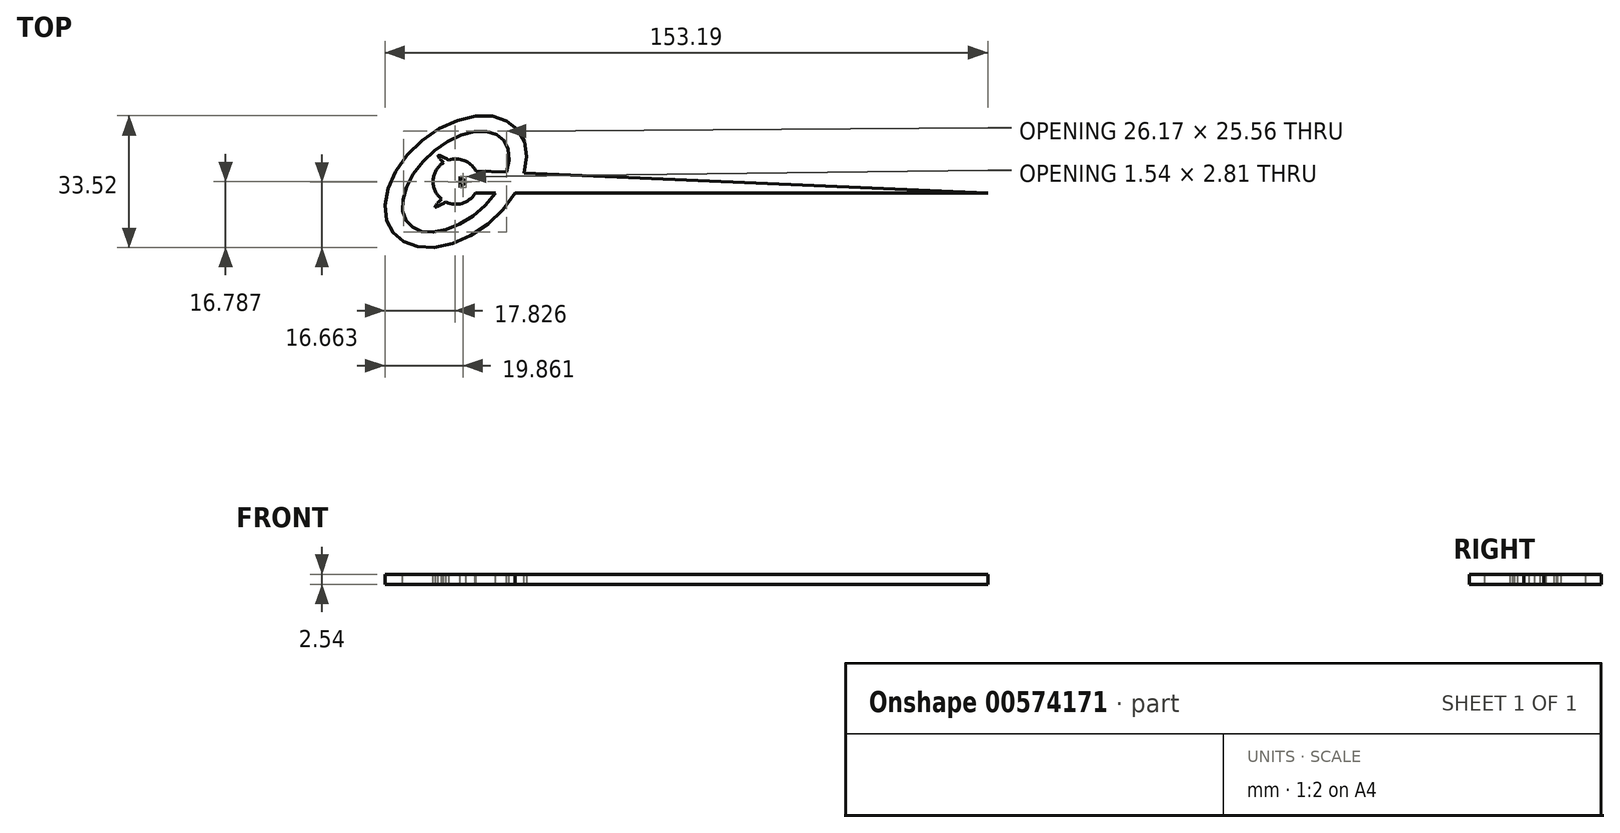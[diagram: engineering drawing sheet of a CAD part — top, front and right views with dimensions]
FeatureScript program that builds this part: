
annotation { "Feature Type Name" : "Feature", "Feature Type Description" : "" }
export const myFeature = defineFeature(function(context is Context, id is Id, definition is map)
    precondition{}
    {
        {
            var Q0;
            Q0=qCreatedBy(makeId("Top.planeOp"),FACE);
            var sketch = newSketch(context, id + "F0", { "sketchPlane" : qUnion([Q0])});
            skLineSegment(sketch, "E0", {"start": v(62.44, 29.81) * mm, "end": v(-67.53, 35.5) * mm});
            skPoint(sketch, "E1.first.point", {"position": v(-72.74, 32.77) * mm});
            skEllipse(sketch, "E2", {"center": v(-72.74, 32.77) * mm, "majorRadius": 20.56 * mm, "minorRadius": 13.51 * mm, "majorAxis": v(-0.77, -0.64)});
            skPoint(sketch, "E3.second.point.positionSnap0", {"position": v(-81.38, 43.15) * mm});
            skEllipse(sketch, "E4", {"center": v(-72.74, 32.77) * mm, "majorRadius": 16.1 * mm, "minorRadius": 9.5 * mm, "majorAxis": v(0.75, 0.67)});
            skFitSpline(sketch, "E5", {"points": [v(-75.87, 37.59) * mm, v(-77.22, 39.4) * mm, v(-74.5, 38.24) * mm], "startDerivative": vector(-4.75, 5.3) * mm, "endDerivative": vector(7.24, -3.82) * mm});
            skFitSpline(sketch, "E6", {"points": [v(-76.39, 28.33) * mm, v(-77.94, 26.33) * mm, v(-75.23, 27.6) * mm], "startDerivative": vector(-5.27, -5.74) * mm, "endDerivative": vector(7.4, 4.13) * mm});
            skLineSegment(sketch, "E7", {"start": v(-71.66, 31.27) * mm, "end": v(-71.66, 34.08) * mm});
            skLineSegment(sketch, "E8", {"start": v(-71.66, 34.08) * mm, "end": v(-70.12, 32.63) * mm});
            skLineSegment(sketch, "E9", {"start": v(-70.12, 32.63) * mm, "end": v(-71.66, 31.27) * mm});
            skLineSegment(sketch, "E10", {"start": v(-67.87, 29.71) * mm, "end": v(-67.64, 29.81) * mm});
            skLineSegment(sketch, "E11.trimOffspring", {"start": v(-67.64, 29.81) * mm, "end": v(62.44, 29.81) * mm});
            skLineSegment(sketch, "E12", {"start": v(-67.75, 35.62) * mm, "end": v(-67.53, 35.5) * mm});
            skArc(sketch, "E13.trimOffspring", {"start": v(-67.75, 35.62) * mm, "mid": v(-78.48, 32.88) * mm, "end": v(-67.87, 29.71) * mm});
            skPoint(sketch, "E14.orphan", {"position": v(-72.66, 35.72) * mm});
            skPoint(sketch, "E15.end.orphan", {"position": v(-72.8, 29.81) * mm});
            skPoint(sketch, "E16.2.internal.orphan", {"position": v(-70.12, 34.46) * mm});
            skPoint(sketch, "E16.startDerivative.orphan", {"position": v(-69.67, 32.96) * mm});
            skPoint(sketch, "E17.2.internal.orphan", {"position": v(-70.12, 30.79) * mm});
            skPoint(sketch, "E18.0.internal.orphan", {"position": v(-69.67, 32.63) * mm});
            skFitSpline(sketch, "E19", {"points": [v(-70.12, 32.63) * mm, v(-69.16, 33.4) * mm, v(-70.33, 34.86) * mm], "startDerivative": vector(3.09, 1.53) * mm, "endDerivative": vector(-3.29, 2.88) * mm});
            skFitSpline(sketch, "E20", {"points": [v(-70.12, 32.63) * mm, v(-69.25, 31.9) * mm, v(-70.23, 30.4) * mm], "startDerivative": vector(2.78, -1.4) * mm, "endDerivative": vector(-2.79, -3.01) * mm});
            skFitSpline(sketch, "E21", {"points": [v(-69.67, 32.63) * mm, v(-68.77, 32.02) * mm, v(-69.92, 30.03) * mm], "startDerivative": vector(3.05, -1.1) * mm, "endDerivative": vector(-3.15, -3.91) * mm});
            skFitSpline(sketch, "E22", {"points": [v(-69.67, 32.63) * mm, v(-68.82, 33.38) * mm, v(-70.2, 35.18) * mm], "startDerivative": vector(2.97, 1.56) * mm, "endDerivative": vector(-3.65, 3.43) * mm});
            skSolve(sketch);
        }
        {
            var Q0;
            {var subQ0=sQuery(id+"F0.wireOp",EDGE,"E0");var subQ1=sQuery(id+"F0.wireOp",EDGE,"IcqNIeTD-ZECF-q0YG-0frz-Qsa368bnDGnI");var subQ2=makeQuery(id+"F0.imprint","INTERSECT",VERTEX,{"derivedFrom":[subQ1,subQ0]});Q0=makeQuery(id+"F0.imprint","IMPRINT",FACE,{"disambiguationData":[TD([[makeQuery(id+"F0.imprint","IMPRINT",EDGE,{"disambiguationData":[TD([[subQ2,1.0]])],"derivedFrom":subQ1}),1.0]])]});}
            var Q1;
            {var subQ0=sQuery(id+"F0.wireOp",EDGE,"E2");var subQ1=sQuery(id+"F0.wireOp",EDGE,"IcqNIeTD-ZECF-q0YG-0frz-Qsa368bnDGnI");var subQ2=makeQuery(id+"F0.imprint","INTERSECT",VERTEX,{"derivedFrom":[subQ1,subQ0]});Q1=makeQuery(id+"F0.imprint","IMPRINT",FACE,{"disambiguationData":[TD([[makeQuery(id+"F0.imprint","IMPRINT",EDGE,{"disambiguationData":[TD([[subQ2,1.0]])],"derivedFrom":subQ1}),-1.0]])]});}
            var Q2;
            {var subQ0=sQuery(id+"F0.wireOp",EDGE,"E2");var subQ1=sQuery(id+"F0.wireOp",EDGE,"IcqNIeTD-ZECF-q0YG-0frz-Qsa368bnDGnI");var subQ2=makeQuery(id+"F0.imprint","INTERSECT",VERTEX,{"derivedFrom":[subQ1,subQ0]});Q2=makeQuery(id+"F0.imprint","IMPRINT",FACE,{"disambiguationData":[TD([[makeQuery(id+"F0.imprint","IMPRINT",EDGE,{"disambiguationData":[TD([[subQ2,1.0]])],"derivedFrom":subQ1}),1.0]])]});}
            var Q3;
            {var subQ0=sQuery(id+"F0.wireOp",EDGE,"YC09zkpM-6MoU-lyNe-iY1n-6Od7lSqIglm4");var subQ1=sQuery(id+"F0.wireOp",EDGE,"IcqNIeTD-ZECF-q0YG-0frz-Qsa368bnDGnI");var subQ2=makeQuery(id+"F0.imprint","INTERSECT",VERTEX,{"derivedFrom":[subQ1,subQ0]});Q3=makeQuery(id+"F0.imprint","IMPRINT",FACE,{"disambiguationData":[TD([[makeQuery(id+"F0.imprint","IMPRINT",EDGE,{"disambiguationData":[TD([[subQ2,-1.0]])],"derivedFrom":subQ1}),1.0]])]});}
            var Q4;
            {var subQ5=sQuery(id+"F0.wireOp",EDGE,"E15");Q4=makeQuery(id+"F0.imprint","IMPRINT",FACE,{"disambiguationData":[TD([[makeQuery(id+"F0.imprint","IMPRINT",EDGE,{"derivedFrom":subQ5}),-1.0]])]});}
            var Q5;
            {var subQ0=sQuery(id+"F0.wireOp",EDGE,"E5");Q5=makeQuery(id+"F0.imprint","IMPRINT",FACE,{"disambiguationData":[TD([[makeQuery(id+"F0.imprint","IMPRINT",EDGE,{"derivedFrom":subQ0}),-1.0]])]});}
            var Q6;
            {var subQ0=sQuery(id+"F0.wireOp",EDGE,"E6");Q6=makeQuery(id+"F0.imprint","IMPRINT",FACE,{"disambiguationData":[TD([[makeQuery(id+"F0.imprint","IMPRINT",EDGE,{"derivedFrom":subQ0}),1.0]])]});}
            var Q7;
            {var subQ0=sQuery(id+"F0.wireOp",EDGE,"E15");Q7=makeQuery(id+"F0.imprint","IMPRINT",FACE,{"disambiguationData":[TD([[makeQuery(id+"F0.imprint","IMPRINT",EDGE,{"derivedFrom":subQ0}),1.0]])]});}
            var Q8;
            {var subQ0=sQuery(id+"F0.wireOp",EDGE,"E2");var subQ1=sQuery(id+"F0.wireOp",EDGE,"E0");var subQ2=makeQuery(id+"F0.imprint","INTERSECT",VERTEX,{"derivedFrom":[subQ1,subQ0]});Q8=makeQuery(id+"F0.imprint","IMPRINT",FACE,{"disambiguationData":[TD([[makeQuery(id+"F0.imprint","IMPRINT",EDGE,{"disambiguationData":[TD([[subQ2,-1.0]])],"derivedFrom":subQ1}),-1.0]])]});}
            var Q9;
            {var subQ0=sQuery(id+"F0.wireOp",EDGE,"E2");var subQ1=sQuery(id+"F0.wireOp",EDGE,"E0");var subQ2=makeQuery(id+"F0.imprint","INTERSECT",VERTEX,{"derivedFrom":[subQ1,subQ0]});Q9=makeQuery(id+"F0.imprint","IMPRINT",FACE,{"disambiguationData":[TD([[makeQuery(id+"F0.imprint","IMPRINT",EDGE,{"disambiguationData":[TD([[subQ2,-1.0]])],"derivedFrom":subQ1}),1.0]])]});}
            var Q10;
            {var subQ0=sQuery(id+"F0.wireOp",EDGE,"E11.trimOffspring");var subQ1=sQuery(id+"F0.wireOp",EDGE,"E0");var subQ2=makeQuery(id+"F0.imprint","INTERSECT",VERTEX,{"derivedFrom":[subQ1,subQ0]});Q10=makeQuery(id+"F0.imprint","IMPRINT",FACE,{"disambiguationData":[TD([[makeQuery(id+"F0.imprint","IMPRINT",EDGE,{"disambiguationData":[TD([[subQ2,-1.0]])],"derivedFrom":subQ1}),1.0]])]});}
            var Q11;
            Q11=makeQuery(id+"F0.imprint","IMPRINT",FACE,{"disambiguationData":[TD([[makeQuery(id+"F0.imprint","IMPRINT",EDGE,{"derivedFrom":sQuery(id+"F0.wireOp",EDGE,"E7")}),1.0]])]});
            var Q12;
            Q12=makeQuery(id+"F0.imprint","IMPRINT",FACE,{"disambiguationData":[TD([[makeQuery(id+"F0.imprint","IMPRINT",EDGE,{"derivedFrom":sQuery(id+"F0.wireOp",EDGE,"E17")}),1.0]])]});
            extrude(context, id + "F1", {"entities" : qUnion([Q0, Q1, Q2, Q3, Q4, Q5, Q6, Q7, Q8, Q9, Q10, Q11, Q12]), "oppositeDirection" : true, "depth" : 2.54 * mm, "offsetDistance" : 25.4 * mm});
        }
    });
